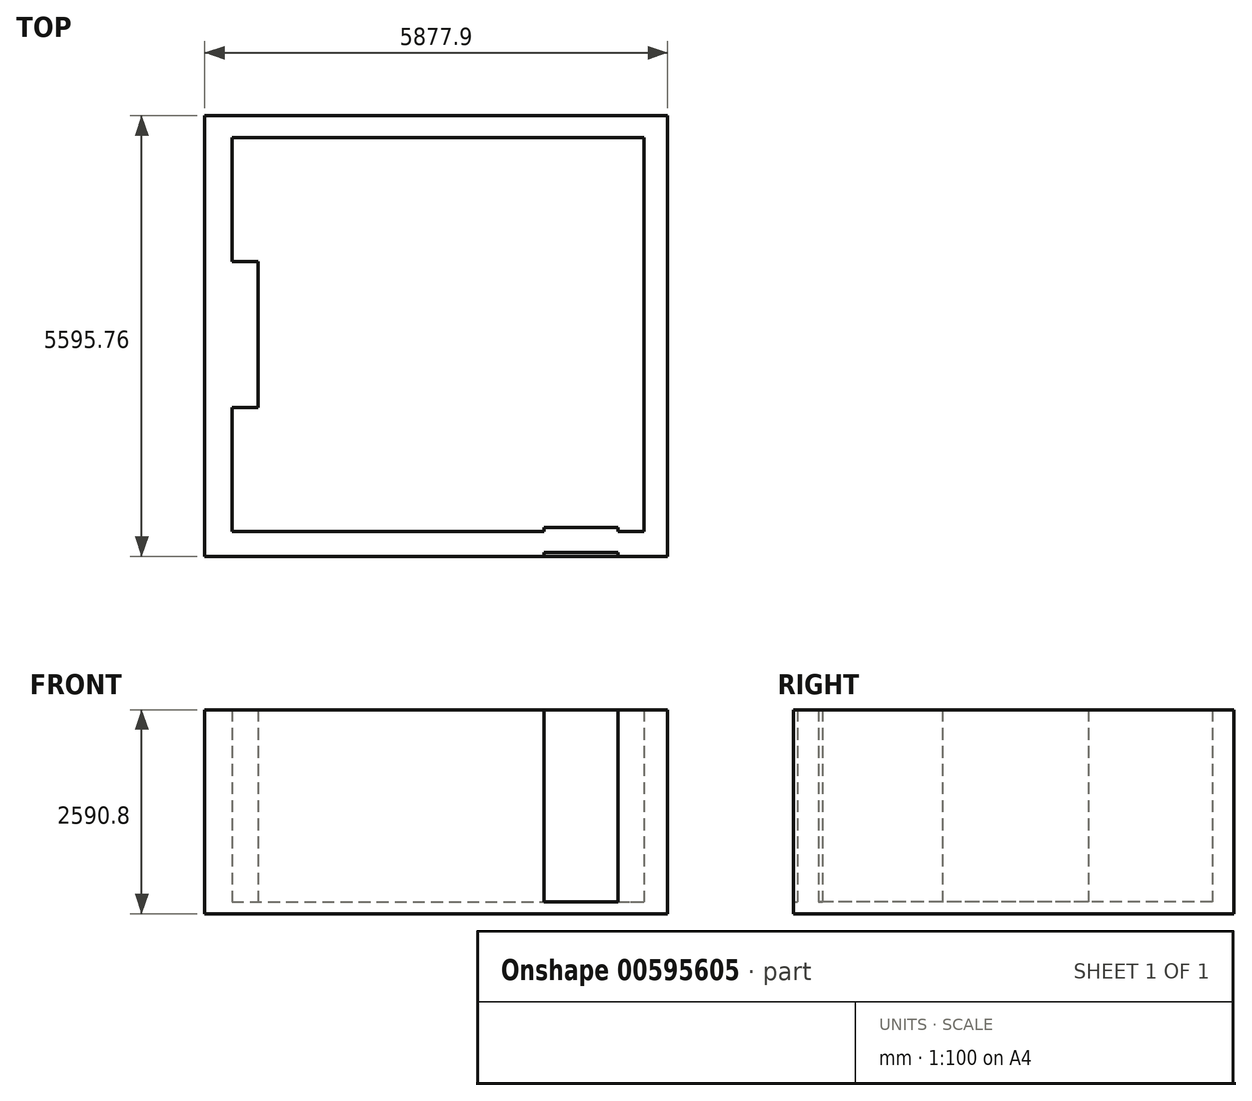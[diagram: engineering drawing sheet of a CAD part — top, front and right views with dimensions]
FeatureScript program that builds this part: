
annotation { "Feature Type Name" : "Feature", "Feature Type Description" : "" }
export const myFeature = defineFeature(function(context is Context, id is Id, definition is map)
    precondition{}
    {
        {
            var Q0;
            Q0=qCreatedBy(makeId("Top.planeOp"),FACE);
            var sketch = newSketch(context, id + "F0", { "sketchPlane" : qUnion([Q0])});
            skLineSegment(sketch, "E0.bottom", {"start": v(-2120.6, 2500.82) * mm, "end": v(3111.8, 2500.82) * mm});
            skLineSegment(sketch, "E0.top", {"start": v(-2120.6, -2502.98) * mm, "end": v(1841.8, -2502.98) * mm});
            skLineSegment(sketch, "E0.left", {"start": v(-2120.6, 2500.82) * mm, "end": v(-2120.6, 926.02) * mm});
            skLineSegment(sketch, "E0.right", {"start": v(3111.8, 2500.82) * mm, "end": v(3111.8, -2502.98) * mm});
            skLineSegment(sketch, "E1.bottom", {"start": v(-2120.6, 926.02) * mm, "end": v(-1790.4, 926.02) * mm});
            skLineSegment(sketch, "E1.top", {"start": v(-2120.6, -928.18) * mm, "end": v(-1790.4, -928.18) * mm});
            skLineSegment(sketch, "E1.right", {"start": v(-1790.4, 926.02) * mm, "end": v(-1790.4, -928.18) * mm});
            skLineSegment(sketch, "E2.trimOffspring", {"start": v(-2120.6, -928.18) * mm, "end": v(-2120.6, -2502.98) * mm});
            skLineSegment(sketch, "E3.top", {"start": v(1841.8, -2452.18) * mm, "end": v(2781.6, -2452.18) * mm});
            skLineSegment(sketch, "E3.left", {"start": v(1841.8, -2502.98) * mm, "end": v(1841.8, -2452.18) * mm});
            skLineSegment(sketch, "E3.right", {"start": v(2781.6, -2502.98) * mm, "end": v(2781.6, -2452.18) * mm});
            skLineSegment(sketch, "E4.trimOffspring", {"start": v(2781.6, -2502.98) * mm, "end": v(3111.8, -2502.98) * mm});
            skLineSegment(sketch, "E5.bottom", {"start": v(-2465.95, 2776.47) * mm, "end": v(3411.95, 2776.47) * mm});
            skLineSegment(sketch, "E5.top", {"start": v(-2465.95, -2819.29) * mm, "end": v(1841.8, -2819.29) * mm});
            skLineSegment(sketch, "E5.left", {"start": v(-2465.95, 2776.47) * mm, "end": v(-2465.95, -2819.29) * mm});
            skLineSegment(sketch, "E5.right", {"start": v(3411.95, 2776.47) * mm, "end": v(3411.95, -2819.29) * mm});
            skLineSegment(sketch, "E6.top", {"start": v(1841.8, -2768.49) * mm, "end": v(2781.6, -2768.49) * mm});
            skLineSegment(sketch, "E6.left", {"start": v(1841.8, -2819.29) * mm, "end": v(1841.8, -2768.49) * mm});
            skLineSegment(sketch, "E6.right", {"start": v(2781.6, -2819.29) * mm, "end": v(2781.6, -2768.49) * mm});
            skLineSegment(sketch, "E7.trimOffspring", {"start": v(2781.6, -2819.29) * mm, "end": v(3411.95, -2819.29) * mm});
            skSolve(sketch);
        }
        {
            var Q0;
            Q0=makeQuery(id+"F0.imprint","IMPRINT",FACE,{"disambiguationData":[TD([[makeQuery(id+"F0.imprint","IMPRINT",EDGE,{"derivedFrom":sQuery(id+"F0.wireOp",EDGE,"E0.bottom")}),1.0]])]});
            extrude(context, id + "F1", {"entities" : qUnion([Q0]), "depth" : 2438.4 * mm, "offsetDistance" : 25.4 * mm});
        }
        {
            var Q0;
            Q0=makeQuery(id+"F1.opExtrude","CAP_FACE",FACE,{"disambiguationData":[OSD([sQuery(id+"F0.wireOp",EDGE,"E0.bottom"),sQuery(id+"F0.wireOp",EDGE,"E0.top"),sQuery(id+"F0.wireOp",EDGE,"E0.left"),sQuery(id+"F0.wireOp",EDGE,"E0.right"),sQuery(id+"F0.wireOp",EDGE,"E1.bottom"),sQuery(id+"F0.wireOp",EDGE,"E1.top"),sQuery(id+"F0.wireOp",EDGE,"E1.right"),sQuery(id+"F0.wireOp",EDGE,"E2.trimOffspring"),sQuery(id+"F0.wireOp",EDGE,"E3.top"),sQuery(id+"F0.wireOp",EDGE,"E3.left"),sQuery(id+"F0.wireOp",EDGE,"E3.right"),sQuery(id+"F0.wireOp",EDGE,"E4.trimOffspring"),sQuery(id+"F0.wireOp",EDGE,"E5.bottom"),sQuery(id+"F0.wireOp",EDGE,"E5.top"),sQuery(id+"F0.wireOp",EDGE,"E5.left"),sQuery(id+"F0.wireOp",EDGE,"E5.right"),sQuery(id+"F0.wireOp",EDGE,"E6.top"),sQuery(id+"F0.wireOp",EDGE,"E6.left"),sQuery(id+"F0.wireOp",EDGE,"E6.right"),sQuery(id+"F0.wireOp",EDGE,"E7.trimOffspring")])],"isStart":true});
            var sketch = newSketch(context, id + "F2", { "sketchPlane" : qUnion([Q0])});
            skLineSegment(sketch, "E8.bottom", {"start": v(-2465.95, 2819.29) * mm, "end": v(3411.95, 2819.29) * mm});
            skLineSegment(sketch, "E8.top", {"start": v(-2465.95, -2776.47) * mm, "end": v(3411.95, -2776.47) * mm});
            skLineSegment(sketch, "E8.left", {"start": v(-2465.95, 2819.29) * mm, "end": v(-2465.95, -2776.47) * mm});
            skLineSegment(sketch, "E8.right", {"start": v(3411.95, 2819.29) * mm, "end": v(3411.95, -2776.47) * mm});
            skSolve(sketch);
        }
        {
            var Q0;
            Q0 = qSketchRegion(id + "F2", true);
            extrude(context, id + "F3", {"entities" : qUnion([Q0]), "operationType" : NewBodyOperationType.ADD, "depth" : 152.4 * mm, "offsetDistance" : 25.4 * mm});
        }
    });
